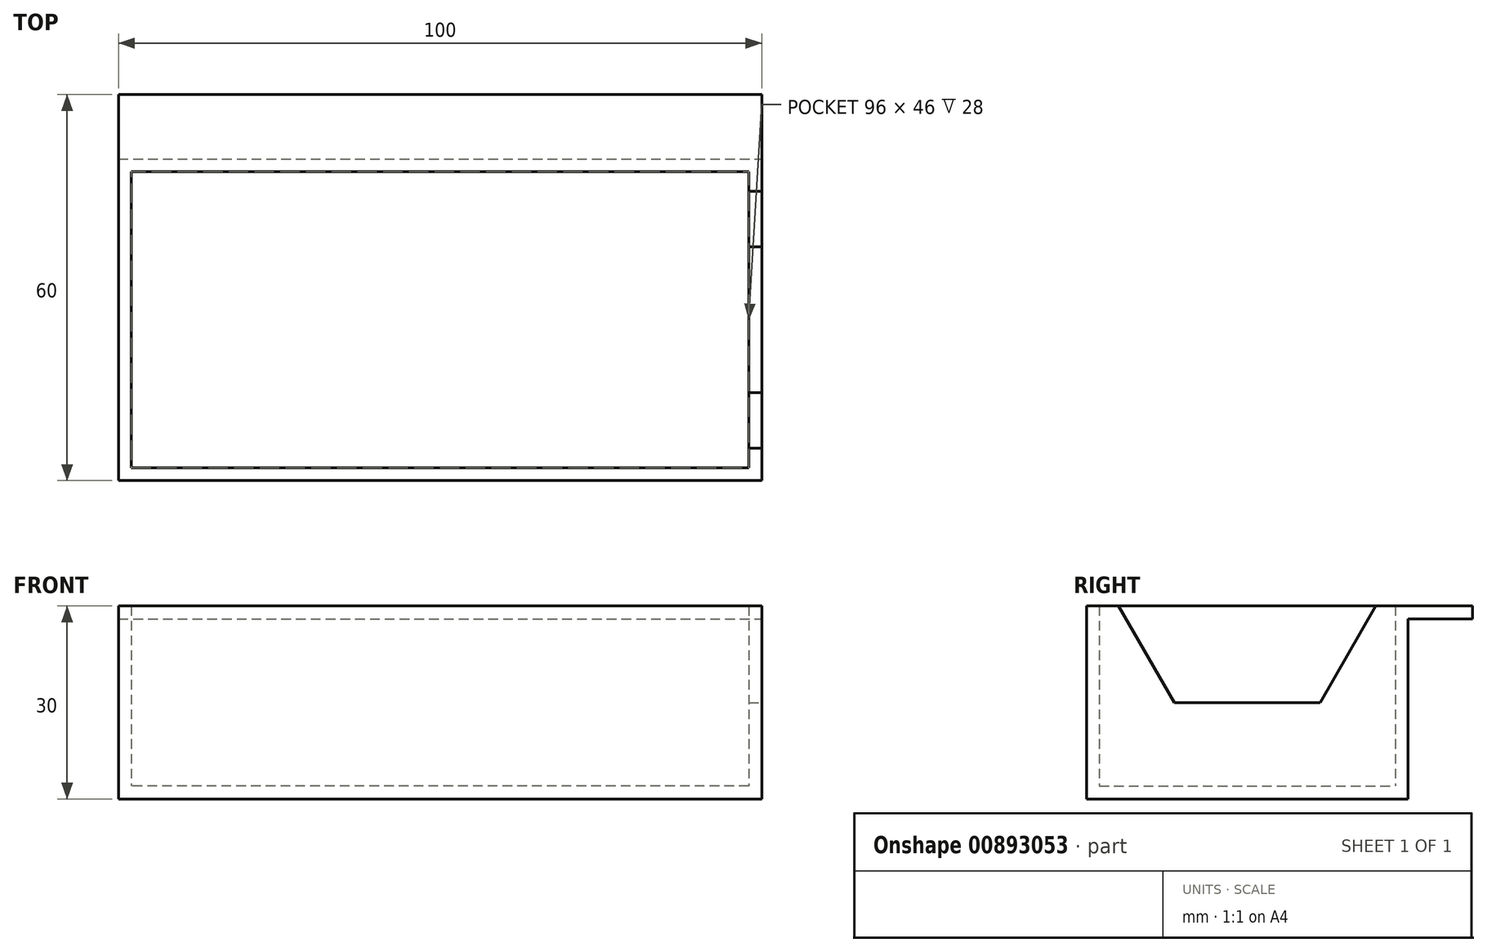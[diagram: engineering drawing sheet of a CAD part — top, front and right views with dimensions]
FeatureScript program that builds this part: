
annotation { "Feature Type Name" : "Feature", "Feature Type Description" : "" }
export const myFeature = defineFeature(function(context is Context, id is Id, definition is map)
    precondition{}
    {
        {
            var Q0;
            Q0=qCreatedBy(makeId("Top.planeOp"),FACE);
            var sketch = newSketch(context, id + "F0", { "sketchPlane" : qUnion([Q0])});
            skLineSegment(sketch, "E0.bottom", {"start": v(50, -25) * mm, "end": v(-50, -25) * mm});
            skLineSegment(sketch, "E0.top", {"start": v(50, 25) * mm, "end": v(-50, 25) * mm});
            skLineSegment(sketch, "E0.left", {"start": v(50, -25) * mm, "end": v(50, 25) * mm});
            skLineSegment(sketch, "E0.right", {"start": v(-50, -25) * mm, "end": v(-50, 25) * mm});
            skPoint(sketch, "E0.middle", {"position": v(0, 0) * mm});
            skSolve(sketch);
        }
        {
            var Q0;
            Q0 = qSketchRegion(id + "F0", true);
            extrude(context, id + "F1", {"entities" : qUnion([Q0]), "depth" : 30 * mm, "offsetDistance" : 25 * mm});
        }
        {
            var Q0;
            Q0=makeQuery(id+"F1.opExtrude","CAP_FACE",FACE,{"disambiguationData":[OSD([sQuery(id+"F0.wireOp",EDGE,"E0.bottom"),sQuery(id+"F0.wireOp",EDGE,"E0.top"),sQuery(id+"F0.wireOp",EDGE,"E0.left"),sQuery(id+"F0.wireOp",EDGE,"E0.right")])],"isStart":false});
            shell(context, id + "F2", {"entities" : qUnion([Q0]), "thickness" : 2 * mm});
        }
        {
            var Q0;
            Q0=makeQuery(id+"F1.opExtrude","SWEPT_FACE",FACE,{"disambiguationData":[OSD([sQuery(id+"F0.wireOp",EDGE,"E0.top")])]});
            var sketch = newSketch(context, id + "F3", { "sketchPlane" : qUnion([Q0])});
            skLineSegment(sketch, "E1.bottom", {"start": v(50, 30) * mm, "end": v(-50, 30) * mm});
            skLineSegment(sketch, "E1.top", {"start": v(50, 28) * mm, "end": v(-50, 28) * mm});
            skLineSegment(sketch, "E1.left", {"start": v(50, 30) * mm, "end": v(50, 28) * mm});
            skLineSegment(sketch, "E1.right", {"start": v(-50, 30) * mm, "end": v(-50, 28) * mm});
            skSolve(sketch);
        }
        {
            var Q0;
            Q0 = qSketchRegion(id + "F3", true);
            extrude(context, id + "F4", {"entities" : qUnion([Q0]), "operationType" : NewBodyOperationType.ADD, "depth" : 10 * mm, "offsetDistance" : 25 * mm});
        }
        {
            var Q0;
            Q0=makeQuery(id+"F1.opExtrude","SWEPT_FACE",FACE,{"disambiguationData":[OSD([sQuery(id+"F0.wireOp",EDGE,"E0.top")])]});
            var Q1;
            Q1=makeQuery(id+"F1.opExtrude","SWEPT_FACE",FACE,{"disambiguationData":[OSD([sQuery(id+"F0.wireOp",EDGE,"E0.bottom")])]});
            cPlane(context, id + "F5", {"entities" : qUnion([Q0, Q1]), "cplaneType" : CPlaneType.MID_PLANE, "offset" : 85 * mm, "width" : 150 * mm, "height" : 150 * mm});
        }
        {
            var Q0;
            {var subQ0=sQuery(id+"F3.wireOp",EDGE,"E1.right");Q0=makeQuery(id+"FzpPQ3Ug2dkogtD_1.1.F4.boolean.opBoolean","MERGE",FACE,{"derivedFrom":[makeQuery(id+"F4.boolean.opBoolean","MERGE",FACE,{"derivedFrom":[makeQuery(id+"F1.opExtrude","SWEPT_FACE",FACE,{"disambiguationData":[OSD([sQuery(id+"F0.wireOp",EDGE,"E0.left")])]}),makeQuery(id+"F4.opExtrude","SWEPT_FACE",FACE,{"disambiguationData":[OSD([subQ0])]})]}),makeQuery(id+"FzpPQ3Ug2dkogtD_1.1.F4.opExtrude","SWEPT_FACE",FACE,{"disambiguationData":[OSD([subQ0])]})]});}
            var sketch = newSketch(context, id + "F6", { "sketchPlane" : qUnion([Q0])});
            skLineSegment(sketch, "E2", {"start": v(20, 30) * mm, "end": v(11.34, 15) * mm});
            skLineSegment(sketch, "E3", {"start": v(11.34, 15) * mm, "end": v(-11.34, 15) * mm});
            skLineSegment(sketch, "E4", {"start": v(-11.34, 15) * mm, "end": v(-20, 30) * mm});
            skLineSegment(sketch, "E5", {"start": v(-20, 30) * mm, "end": v(20, 30) * mm});
            skLineSegment(sketch, "E6", {"start": v(0, -16.92) * mm, "end": v(0, 44.73) * mm, "construction": true});
            skSolve(sketch);
        }
        {
            var Q0;
            Q0 = qSketchRegion(id + "F6", true);
            extrude(context, id + "F7", {"entities" : qUnion([Q0]), "operationType" : NewBodyOperationType.REMOVE, "endBound" : BoundingType.UP_TO_NEXT, "oppositeDirection" : true, "depth" : 25 * mm, "offsetDistance" : 25 * mm});
        }
    });
